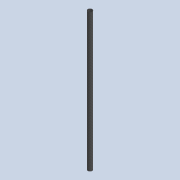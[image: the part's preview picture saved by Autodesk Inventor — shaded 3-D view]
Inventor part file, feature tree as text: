
AUTODESK INVENTOR PART (.ipt)
format: ipt  version: 2020 (Build 240168000, 168)  size: 75,264 bytes
history: native  units: mm
features: extrude x1, sketch x1
ambient origin geometry x8: Origin, YZ Plane, XZ Plane, XY Plane, X Axis, Y Axis, Z Axis, Center Point
bodies: Solid1 (feature_tree)
feature tree (2):
  extrude  "Extrusion1"  Depth=800.0mm
  sketch  "Sketch1"  dims[d0=25.0mm d1=22.0mm d2=800.0mm d3=0.0mm]
